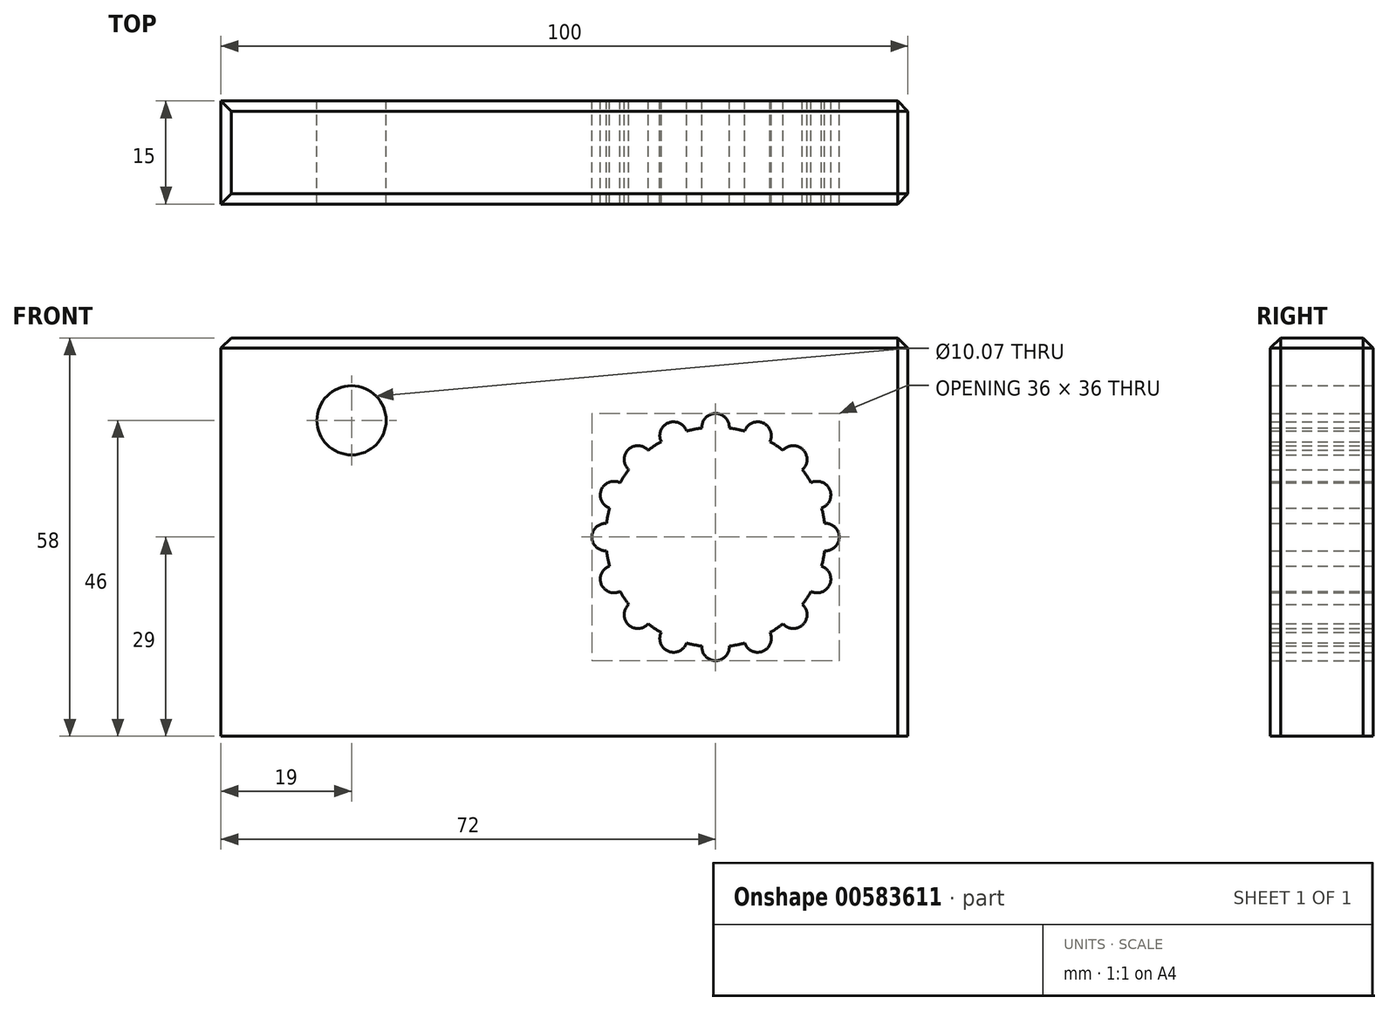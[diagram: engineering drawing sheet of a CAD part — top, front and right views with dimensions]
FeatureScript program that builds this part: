
annotation { "Feature Type Name" : "Feature", "Feature Type Description" : "" }
export const myFeature = defineFeature(function(context is Context, id is Id, definition is map)
    precondition{}
    {
        {
            var Q0;
            Q0=qCreatedBy(makeId("Front.planeOp"),FACE);
            var sketch = newSketch(context, id + "F0", { "sketchPlane" : qUnion([Q0])});
            skLineSegment(sketch, "E0.bottom", {"start": v(50, -29) * mm, "end": v(-50, -29) * mm});
            skLineSegment(sketch, "E0.top", {"start": v(50, 29) * mm, "end": v(-50, 29) * mm});
            skLineSegment(sketch, "E0.left", {"start": v(50, -29) * mm, "end": v(50, 29) * mm});
            skLineSegment(sketch, "E0.right", {"start": v(-50, -29) * mm, "end": v(-50, 29) * mm});
            skPoint(sketch, "E0.middle", {"position": v(0, 0) * mm});
            skCircle(sketch, "E1", {"center": v(-31, 17) * mm, "radius": 5.03 * mm});
            skArc(sketch, "E2", {"start": v(9.36, 9.81) * mm, "mid": v(8.7, 8.89) * mm, "end": v(8.1, 7.92) * mm});
            skArc(sketch, "E3", {"start": v(6.13, 2) * mm, "mid": v(4, 0) * mm, "end": v(6.13, -2) * mm});
            skArc(sketch, "E4", {"start": v(37.88, -2) * mm, "mid": v(40, 0) * mm, "end": v(37.88, 2) * mm});
            skArc(sketch, "E5", {"start": v(20, -15.88) * mm, "mid": v(22, -18) * mm, "end": v(24, -15.88) * mm});
            skArc(sketch, "E6", {"start": v(24, 15.88) * mm, "mid": v(22, 18) * mm, "end": v(20, 15.88) * mm});
            skArc(sketch, "E7", {"start": v(29.92, 13.9) * mm, "mid": v(28.89, 16.63) * mm, "end": v(26.23, 15.43) * mm});
            skArc(sketch, "E8", {"start": v(34.64, 9.81) * mm, "mid": v(34.73, 12.73) * mm, "end": v(31.81, 12.64) * mm});
            skArc(sketch, "E9", {"start": v(37.43, 4.23) * mm, "mid": v(38.63, 6.89) * mm, "end": v(35.9, 7.92) * mm});
            skArc(sketch, "E10", {"start": v(35.9, -7.92) * mm, "mid": v(38.63, -6.89) * mm, "end": v(37.43, -4.23) * mm});
            skArc(sketch, "E11", {"start": v(31.81, -12.64) * mm, "mid": v(34.73, -12.73) * mm, "end": v(34.64, -9.81) * mm});
            skArc(sketch, "E12", {"start": v(26.23, -15.43) * mm, "mid": v(28.89, -16.63) * mm, "end": v(29.92, -13.9) * mm});
            skArc(sketch, "E13", {"start": v(14.08, -13.9) * mm, "mid": v(15.11, -16.63) * mm, "end": v(17.77, -15.43) * mm});
            skArc(sketch, "E14", {"start": v(9.36, -9.81) * mm, "mid": v(9.27, -12.73) * mm, "end": v(12.19, -12.64) * mm});
            skArc(sketch, "E15", {"start": v(6.57, -4.23) * mm, "mid": v(5.37, -6.89) * mm, "end": v(8.1, -7.92) * mm});
            skArc(sketch, "E16", {"start": v(8.1, 7.92) * mm, "mid": v(5.37, 6.89) * mm, "end": v(6.57, 4.23) * mm});
            skArc(sketch, "E17", {"start": v(12.19, 12.64) * mm, "mid": v(9.27, 12.73) * mm, "end": v(9.36, 9.81) * mm});
            skArc(sketch, "E18", {"start": v(17.77, 15.43) * mm, "mid": v(15.11, 16.63) * mm, "end": v(14.08, 13.9) * mm});
            skArc(sketch, "E19.trimOffspring", {"start": v(6.57, 4.23) * mm, "mid": v(6.3, 3.12) * mm, "end": v(6.13, 2) * mm});
            skArc(sketch, "E20.trimOffspring", {"start": v(6.13, -2) * mm, "mid": v(6.3, -3.12) * mm, "end": v(6.57, -4.23) * mm});
            skArc(sketch, "E21.trimOffspring", {"start": v(8.1, -7.92) * mm, "mid": v(8.7, -8.89) * mm, "end": v(9.36, -9.81) * mm});
            skArc(sketch, "E22.trimOffspring", {"start": v(12.19, -12.64) * mm, "mid": v(13.11, -13.3) * mm, "end": v(14.08, -13.9) * mm});
            skArc(sketch, "E23.trimOffspring", {"start": v(17.77, -15.43) * mm, "mid": v(18.88, -15.7) * mm, "end": v(20, -15.88) * mm});
            skArc(sketch, "E24.trimOffspring", {"start": v(24, -15.88) * mm, "mid": v(25.12, -15.7) * mm, "end": v(26.23, -15.43) * mm});
            skArc(sketch, "E25.trimOffspring", {"start": v(29.92, -13.9) * mm, "mid": v(30.89, -13.3) * mm, "end": v(31.81, -12.64) * mm});
            skArc(sketch, "E26.trimOffspring", {"start": v(34.64, -9.81) * mm, "mid": v(35.3, -8.89) * mm, "end": v(35.9, -7.92) * mm});
            skArc(sketch, "E27.trimOffspring", {"start": v(37.43, -4.23) * mm, "mid": v(37.7, -3.12) * mm, "end": v(37.88, -2) * mm});
            skArc(sketch, "E28.trimOffspring", {"start": v(37.88, 2) * mm, "mid": v(37.7, 3.12) * mm, "end": v(37.43, 4.23) * mm});
            skArc(sketch, "E29.trimOffspring", {"start": v(31.81, 12.64) * mm, "mid": v(30.89, 13.3) * mm, "end": v(29.92, 13.9) * mm});
            skArc(sketch, "E30.trimOffspring", {"start": v(26.23, 15.43) * mm, "mid": v(25.12, 15.7) * mm, "end": v(24, 15.88) * mm});
            skArc(sketch, "E31.trimOffspring", {"start": v(20, 15.88) * mm, "mid": v(18.88, 15.7) * mm, "end": v(17.77, 15.43) * mm});
            skArc(sketch, "E32.trimOffspring", {"start": v(14.08, 13.9) * mm, "mid": v(13.11, 13.3) * mm, "end": v(12.19, 12.64) * mm});
            skArc(sketch, "E33.trimOffspring", {"start": v(35.9, 7.92) * mm, "mid": v(35.3, 8.89) * mm, "end": v(34.64, 9.81) * mm});
            skSolve(sketch);
        }
        {
            var Q0;
            Q0=makeQuery(id+"F0.imprint","IMPRINT",FACE,{"disambiguationData":[TD([[makeQuery(id+"F0.imprint","IMPRINT",EDGE,{"derivedFrom":sQuery(id+"F0.wireOp",EDGE,"E0.bottom")}),-1.0]])]});
            extrude(context, id + "F1", {"entities" : qUnion([Q0]), "depth" : 15 * mm, "offsetDistance" : 25.4 * mm, "symmetric" : true});
        }
        {
            var Q0;
            Q0=makeQuery(id+"F1.opExtrude","SWEPT_EDGE",EDGE,{"disambiguationData":[OSD([sQuery(id+"F0.wireOp",EDGE,"E0.top"),sQuery(id+"F0.wireOp",EDGE,"E0.left")])]});
            var Q1;
            Q1=makeQuery(id+"F1.opExtrude","CAP_EDGE",EDGE,{"disambiguationData":[OSD([sQuery(id+"F0.wireOp",EDGE,"E0.top")])],"isStart":true});
            var Q2;
            Q2=makeQuery(id+"F1.opExtrude","CAP_EDGE",EDGE,{"disambiguationData":[OSD([sQuery(id+"F0.wireOp",EDGE,"E0.top")])],"isStart":false});
            var Q3;
            Q3=makeQuery(id+"F1.opExtrude","CAP_EDGE",EDGE,{"disambiguationData":[OSD([sQuery(id+"F0.wireOp",EDGE,"E0.left")])],"isStart":false});
            var Q4;
            Q4=makeQuery(id+"F1.opExtrude","CAP_EDGE",EDGE,{"disambiguationData":[OSD([sQuery(id+"F0.wireOp",EDGE,"E0.left")])],"isStart":true});
            var Q5;
            Q5=makeQuery(id+"F1.opExtrude","SWEPT_EDGE",EDGE,{"disambiguationData":[OSD([sQuery(id+"F0.wireOp",EDGE,"E0.top"),sQuery(id+"F0.wireOp",EDGE,"E0.right")])]});
            chamfer(context, id + "F2", {"entities" : qUnion([Q0, Q1, Q2, Q3, Q4, Q5]), "width" : 1.5 * mm, "tangentPropagation" : true});
        }
    });
